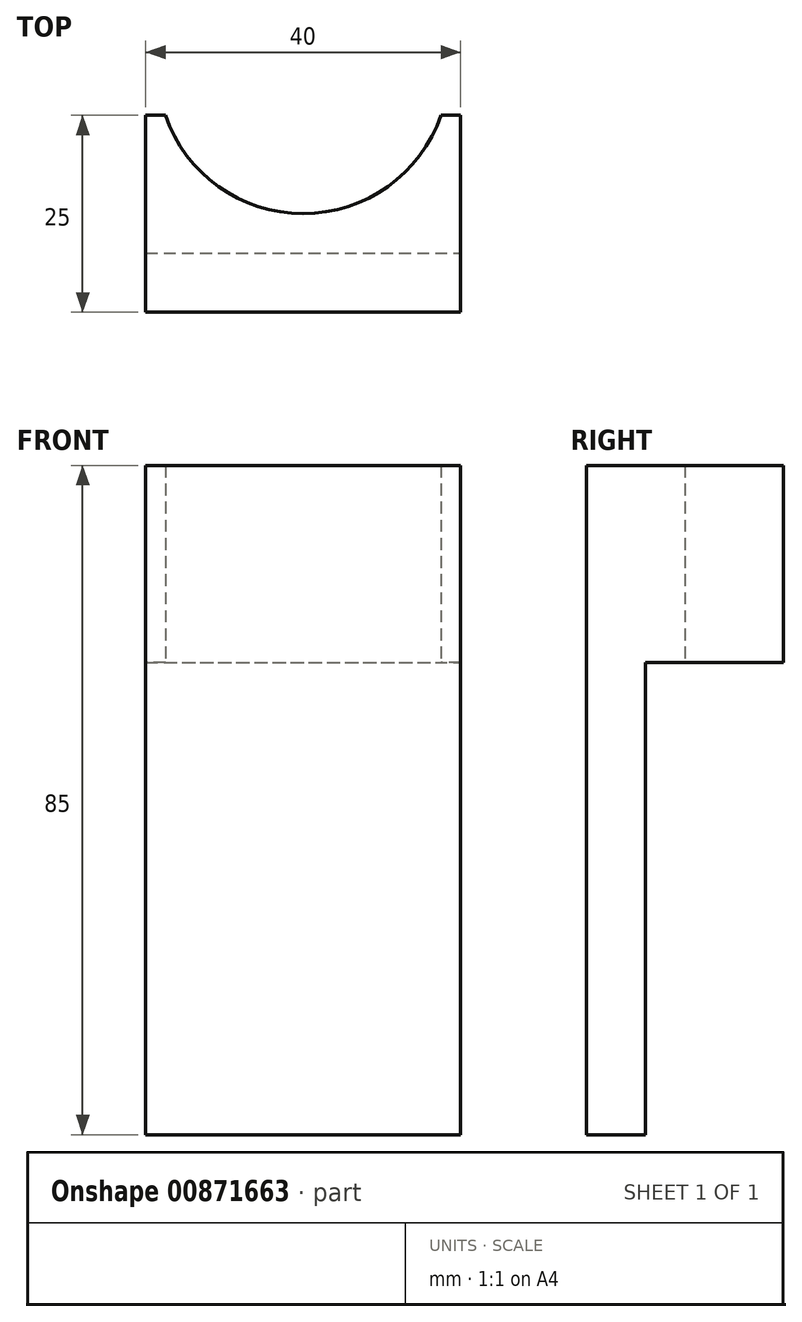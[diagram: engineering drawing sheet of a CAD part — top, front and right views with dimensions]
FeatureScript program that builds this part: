
annotation { "Feature Type Name" : "Feature", "Feature Type Description" : "" }
export const myFeature = defineFeature(function(context is Context, id is Id, definition is map)
    precondition{}
    {
        {
            var Q0;
            Q0=qCreatedBy(makeId("Top.planeOp"),FACE);
            var sketch = newSketch(context, id + "F0", { "sketchPlane" : qUnion([Q0])});
            skCircle(sketch, "E0", {"center": v(0, 0) * mm, "radius": 18.5 * mm});
            skLineSegment(sketch, "E1.bottom", {"start": v(20, -6) * mm, "end": v(-20, -6) * mm});
            skLineSegment(sketch, "E1.top", {"start": v(20, -31) * mm, "end": v(-20, -31) * mm});
            skLineSegment(sketch, "E1.left", {"start": v(20, -6) * mm, "end": v(20, -31) * mm});
            skLineSegment(sketch, "E1.right", {"start": v(-20, -6) * mm, "end": v(-20, -31) * mm});
            skPoint(sketch, "E1.middle", {"position": v(0, -18.5) * mm});
            skSolve(sketch);
        }
        {
            var Q0;
            Q0=makeQuery(id+"F0.imprint","IMPRINT",FACE,{"disambiguationData":[TD([[makeQuery(id+"F0.imprint","IMPRINT",EDGE,{"derivedFrom":sQuery(id+"F0.wireOp",EDGE,"E1.top")}),-1.0]])]});
            extrude(context, id + "F1", {"entities" : qUnion([Q0]), "depth" : 25 * mm, "offsetDistance" : 25 * mm});
        }
        {
            var Q0;
            Q0=makeQuery(id+"F1.opExtrude","CAP_FACE",FACE,{"disambiguationData":[OSD([sQuery(id+"F0.wireOp",EDGE,"E0"),sQuery(id+"F0.wireOp",EDGE,"E1.bottom"),sQuery(id+"F0.wireOp",EDGE,"E1.top"),sQuery(id+"F0.wireOp",EDGE,"E1.left"),sQuery(id+"F0.wireOp",EDGE,"E1.right")])],"isStart":true});
            var sketch = newSketch(context, id + "F2", { "sketchPlane" : qUnion([Q0])});
            skLineSegment(sketch, "E2.bottom", {"start": v(-20, 31) * mm, "end": v(20, 31) * mm});
            skLineSegment(sketch, "E2.top", {"start": v(-20, 18.5) * mm, "end": v(20, 18.5) * mm});
            skLineSegment(sketch, "E2.left", {"start": v(-20, 31) * mm, "end": v(-20, 18.5) * mm});
            skLineSegment(sketch, "E2.right", {"start": v(20, 31) * mm, "end": v(20, 18.5) * mm});
            skSolve(sketch);
        }
        {
            var Q0;
            Q0 = qSketchRegion(id + "F2", true);
            extrude(context, id + "F3", {"entities" : qUnion([Q0]), "operationType" : NewBodyOperationType.ADD, "depth" : 35 * mm, "offsetDistance" : 25 * mm});
        }
        {
            var Q0;
            Q0=makeQuery(id+"F3.opExtrude","CAP_FACE",FACE,{"disambiguationData":[OSD([sQuery(id+"F2.wireOp",EDGE,"E2.bottom"),sQuery(id+"F2.wireOp",EDGE,"E2.top"),sQuery(id+"F2.wireOp",EDGE,"E2.left"),sQuery(id+"F2.wireOp",EDGE,"E2.right")])],"isStart":false});
            var sketch = newSketch(context, id + "F4", { "sketchPlane" : qUnion([Q0])});
            skCircle(sketch, "E3", {"center": v(0, 0) * mm, "radius": 18.5 * mm});
            skLineSegment(sketch, "E4.bottom", {"start": v(-20, 31) * mm, "end": v(20, 31) * mm});
            skLineSegment(sketch, "E4.top", {"start": v(-20, 6) * mm, "end": v(20, 6) * mm});
            skLineSegment(sketch, "E4.left", {"start": v(-20, 31) * mm, "end": v(-20, 6) * mm});
            skLineSegment(sketch, "E4.right", {"start": v(20, 31) * mm, "end": v(20, 6) * mm});
            skSolve(sketch);
        }
        {
            var Q0;
            {var subQ0=sQuery(id+"F4.wireOp",EDGE,"E4.top");var subQ1=sQuery(id+"F4.wireOp",EDGE,"E3");var subQ2=makeQuery(id+"F4.imprint","INTERSECT",VERTEX,{"disambiguationData":[OD(1.0)],"derivedFrom":[subQ1,subQ0]});Q0=makeQuery(id+"F4.imprint","IMPRINT",FACE,{"disambiguationData":[TD([[makeQuery(id+"F4.imprint","IMPRINT",EDGE,{"disambiguationData":[TD([[subQ2,1.0]])],"derivedFrom":subQ1}),-1.0]])]});}
            var Q1;
            {var subQ5=sQuery(id+"F4.wireOp",EDGE,"E4.bottom");Q1=makeQuery(id+"F4.imprint","IMPRINT",FACE,{"disambiguationData":[TD([[makeQuery(id+"F4.imprint","IMPRINT",EDGE,{"derivedFrom":subQ5}),1.0]])]});}
            var Q2;
            {var subQ0=sQuery(id+"F4.wireOp",EDGE,"E4.top");var subQ1=sQuery(id+"F4.wireOp",EDGE,"E3");var subQ2=makeQuery(id+"F4.imprint","INTERSECT",VERTEX,{"disambiguationData":[OD(0.0)],"derivedFrom":[subQ1,subQ0]});Q2=makeQuery(id+"F4.imprint","IMPRINT",FACE,{"disambiguationData":[TD([[makeQuery(id+"F4.imprint","IMPRINT",EDGE,{"disambiguationData":[TD([[subQ2,-1.0]])],"derivedFrom":subQ1}),-1.0]])]});}
            extrude(context, id + "F5", {"entities" : qUnion([Q0, Q1, Q2]), "operationType" : NewBodyOperationType.ADD, "depth" : 25 * mm, "offsetDistance" : 25 * mm});
        }
        {
            var Q0;
            Q0=makeQuery(id+"F3.opExtrude","SWEPT_FACE",FACE,{"disambiguationData":[OSD([sQuery(id+"F2.wireOp",EDGE,"E2.top")])]});
            extrude(context, id + "F6", {"entities" : qUnion([Q0]), "operationType" : NewBodyOperationType.REMOVE, "oppositeDirection" : true, "depth" : 5 * mm, "offsetDistance" : 25 * mm});
        }
    });
